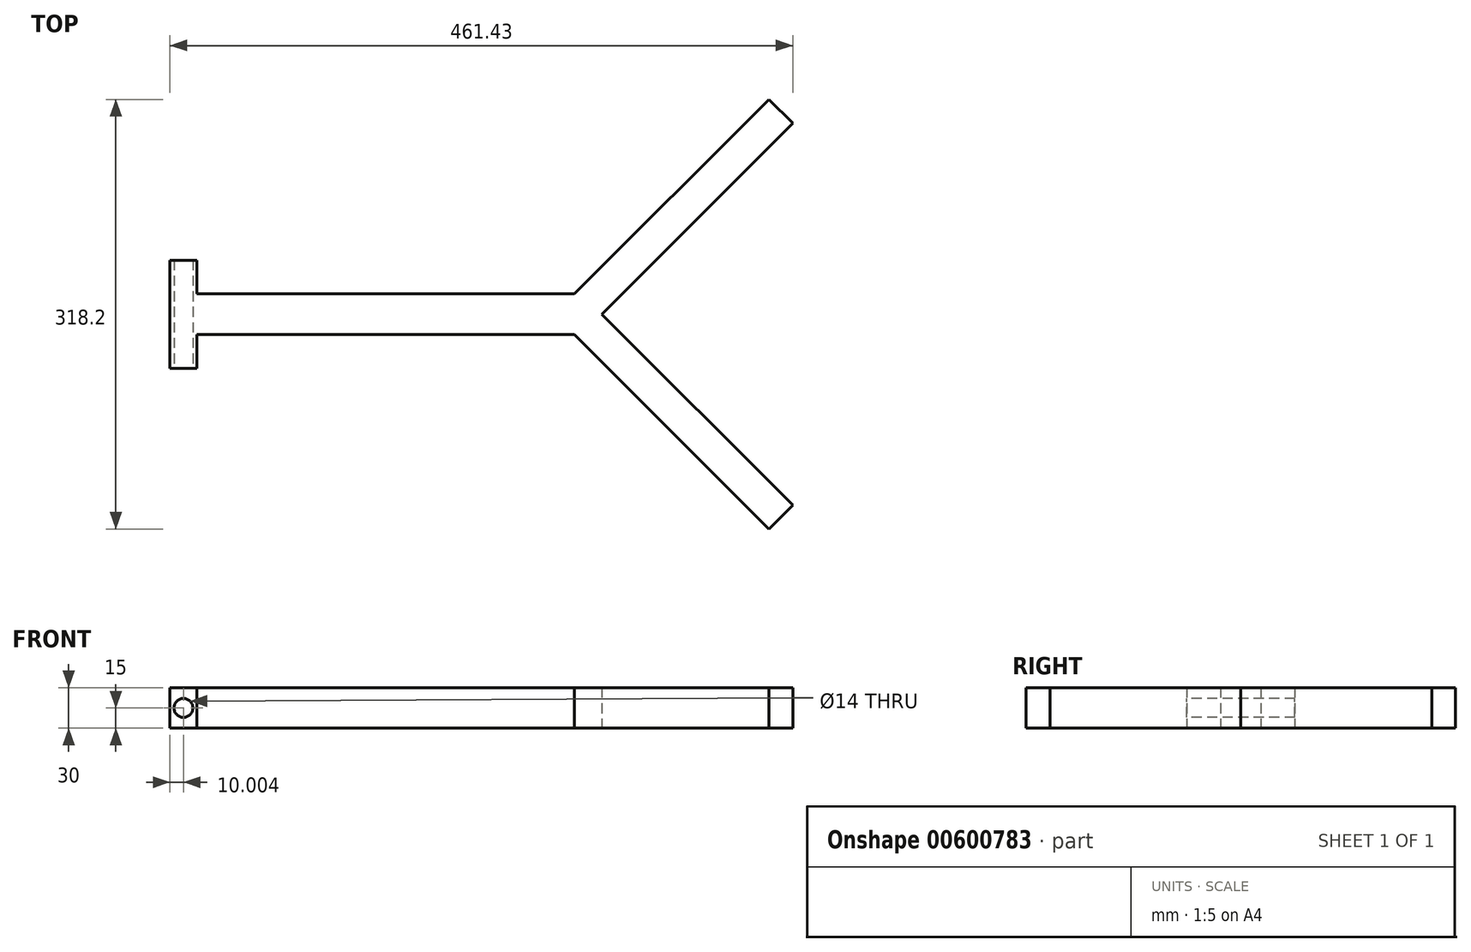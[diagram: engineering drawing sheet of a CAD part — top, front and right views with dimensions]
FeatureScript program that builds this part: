
annotation { "Feature Type Name" : "Feature", "Feature Type Description" : "" }
export const myFeature = defineFeature(function(context is Context, id is Id, definition is map)
    precondition{}
    {
        {
            var Q0;
            Q0=qCreatedBy(makeId("Top.planeOp"),FACE);
            var sketch = newSketch(context, id + "F0", { "sketchPlane" : qUnion([Q0])});
            skLineSegment(sketch, "E0.left", {"start": v(-106.6, 12.34) * mm, "end": v(-106.6, -17.66) * mm});
            skLineSegment(sketch, "E1", {"start": v(193.4, -2.66) * mm, "end": v(334.82, 138.76) * mm});
            skLineSegment(sketch, "E2", {"start": v(334.82, 138.76) * mm, "end": v(317.14, 156.44) * mm});
            skLineSegment(sketch, "E3", {"start": v(317.14, 156.44) * mm, "end": v(173.04, 12.34) * mm});
            skLineSegment(sketch, "E4", {"start": v(193.4, -2.66) * mm, "end": v(334.82, -144.08) * mm});
            skLineSegment(sketch, "E5", {"start": v(334.82, -144.08) * mm, "end": v(317.14, -161.76) * mm});
            skLineSegment(sketch, "E6", {"start": v(317.14, -161.76) * mm, "end": v(173.04, -17.66) * mm});
            skLineSegment(sketch, "E7.bottom", {"start": v(-106.6, -42.66) * mm, "end": v(-126.6, -42.66) * mm});
            skLineSegment(sketch, "E7.top", {"start": v(-106.6, 37.34) * mm, "end": v(-126.6, 37.34) * mm});
            skLineSegment(sketch, "E7.left", {"start": v(-106.6, -42.66) * mm, "end": v(-106.6, 37.34) * mm});
            skLineSegment(sketch, "E7.right", {"start": v(-126.6, -42.66) * mm, "end": v(-126.6, 37.34) * mm});
            skLineSegment(sketch, "E8", {"start": v(-106.6, 12.34) * mm, "end": v(173.04, 12.34) * mm});
            skLineSegment(sketch, "E9", {"start": v(173.04, -17.66) * mm, "end": v(-106.6, -17.66) * mm});
            skSolve(sketch);
        }
        {
            var Q0;
            Q0 = qSketchRegion(id + "F0", true);
            extrude(context, id + "F1", {"entities" : qUnion([Q0]), "depth" : 30 * mm, "offsetDistance" : 25 * mm});
        }
        {
            var Q0;
            Q0=makeQuery(id+"F1.opExtrude","SWEPT_FACE",FACE,{"disambiguationData":[OSD([sQuery(id+"F0.wireOp",EDGE,"E7.bottom")])]});
            var sketch = newSketch(context, id + "F2", { "sketchPlane" : qUnion([Q0])});
            skLineSegment(sketch, "E10", {"start": v(-126.6, 15) * mm, "end": v(-106.6, 15) * mm});
            skLineSegment(sketch, "E11", {"start": v(-116.6, 0) * mm, "end": v(-116.6, 30) * mm});
            skCircle(sketch, "E12", {"center": v(-116.6, 15) * mm, "radius": 7 * mm});
            skSolve(sketch);
        }
        {
            var Q0;
            Q0=sQuery(id+"F2.wireOp",VERTEX,"E12.center");
            var Q1;
            Q1=makeQuery(id+"F1.opExtrude","SWEPT_BODY",BODY,{"disambiguationData":[OSD([sQuery(id+"F0.wireOp",EDGE,"E0.bottom"),sQuery(id+"F0.wireOp",EDGE,"E0.top"),sQuery(id+"F0.wireOp",EDGE,"E1"),sQuery(id+"F0.wireOp",EDGE,"E2"),sQuery(id+"F0.wireOp",EDGE,"E3"),sQuery(id+"F0.wireOp",EDGE,"E4"),sQuery(id+"F0.wireOp",EDGE,"E5"),sQuery(id+"F0.wireOp",EDGE,"E6"),sQuery(id+"F0.wireOp",EDGE,"E7.bottom"),sQuery(id+"F0.wireOp",EDGE,"E7.top"),sQuery(id+"F0.wireOp",EDGE,"E7.left"),sQuery(id+"F0.wireOp",EDGE,"E7.right")])]});
            hole(context, id + "F3", {"style" : HoleStyle.SIMPLE, "endStyle" : HoleEndStyle.THROUGH, "holeDiameter" : 14 * mm, "majorDiameter" : 5 * mm, "isTappedThrough" : true, "tappedDepth" : 12 * mm, "tapClearance" : 3, "locations" : qUnion([Q0]), "scope" : qUnion([Q1])});
        }
    });
